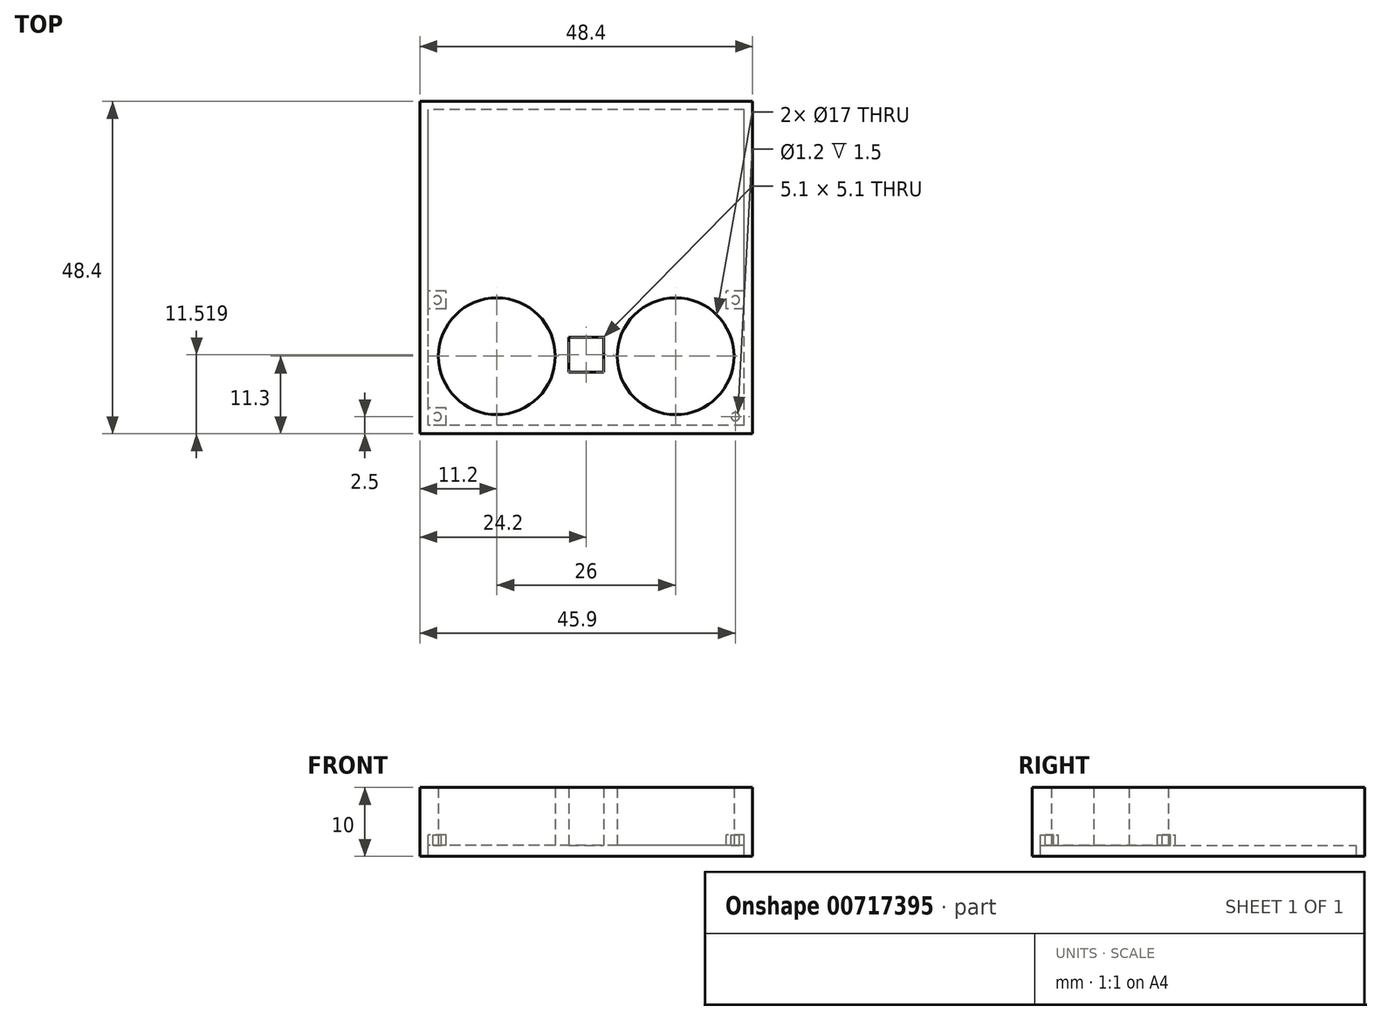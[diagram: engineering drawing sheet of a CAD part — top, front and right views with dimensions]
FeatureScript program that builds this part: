
annotation { "Feature Type Name" : "Feature", "Feature Type Description" : "" }
export const myFeature = defineFeature(function(context is Context, id is Id, definition is map)
    precondition{}
    {
        {
            var Q0;
            Q0=qCreatedBy(makeId("Top.planeOp"),FACE);
            var sketch = newSketch(context, id + "F0", { "sketchPlane" : qUnion([Q0])});
            skLineSegment(sketch, "E0.bottom", {"start": v(0, 0) * mm, "end": v(-23, 0) * mm});
            skLineSegment(sketch, "E0.top", {"start": v(0, 23) * mm, "end": v(-23, 23) * mm});
            skLineSegment(sketch, "E0.left", {"start": v(0, 0) * mm, "end": v(0, 23) * mm});
            skLineSegment(sketch, "E0.right", {"start": v(-23, 0) * mm, "end": v(-23, 23) * mm});
            skLineSegment(sketch, "E1.MirrorCS", {"start": v(-23, 0) * mm, "end": v(-23, -23) * mm});
            skLineSegment(sketch, "E2.MirrorCS", {"start": v(0, 0) * mm, "end": v(0, -23) * mm});
            skLineSegment(sketch, "E3.MirrorCS", {"start": v(0, -23) * mm, "end": v(-23, -23) * mm});
            skLineSegment(sketch, "E4.MirrorCS", {"start": v(0, 23) * mm, "end": v(23, 23) * mm});
            skLineSegment(sketch, "E5.MirrorCS", {"start": v(0, -23) * mm, "end": v(23, -23) * mm});
            skLineSegment(sketch, "E6.MirrorCS", {"start": v(23, 0) * mm, "end": v(23, 23) * mm});
            skLineSegment(sketch, "E7.MirrorCS", {"start": v(0, 0) * mm, "end": v(23, 0) * mm});
            skLineSegment(sketch, "E8.MirrorCS", {"start": v(23, 0) * mm, "end": v(23, -23) * mm});
            skCircle(sketch, "E9", {"center": v(13, -12.9) * mm, "radius": 8.5 * mm});
            skCircle(sketch, "E10", {"center": v(-13, -12.9) * mm, "radius": 8.5 * mm});
            skLineSegment(sketch, "E11.bottom", {"start": v(-2.55, -15.23) * mm, "end": v(2.55, -15.23) * mm});
            skLineSegment(sketch, "E11.top", {"start": v(-2.55, -10.13) * mm, "end": v(2.55, -10.13) * mm});
            skLineSegment(sketch, "E11.left", {"start": v(-2.55, -15.23) * mm, "end": v(-2.55, -10.13) * mm});
            skLineSegment(sketch, "E11.right", {"start": v(2.55, -15.23) * mm, "end": v(2.55, -10.13) * mm});
            skSolve(sketch);
        }
        {
            var Q0;
            {var subQ1=sQuery(id+"F0.wireOp",EDGE,"E0.top");Q0=makeQuery(id+"F0.imprint","IMPRINT",FACE,{"disambiguationData":[TD([[makeQuery(id+"F0.imprint","IMPRINT",EDGE,{"derivedFrom":subQ1}),1.0]])]});}
            var Q1;
            {var subQ1=sQuery(id+"F0.wireOp",EDGE,"E1.MirrorCS");Q1=makeQuery(id+"F0.imprint","IMPRINT",FACE,{"disambiguationData":[TD([[makeQuery(id+"F0.imprint","IMPRINT",EDGE,{"derivedFrom":subQ1}),1.0]])]});}
            var Q2;
            {var subQ7=sQuery(id+"F0.wireOp",EDGE,"E4.MirrorCS");Q2=makeQuery(id+"F0.imprint","IMPRINT",FACE,{"disambiguationData":[TD([[makeQuery(id+"F0.imprint","IMPRINT",EDGE,{"derivedFrom":subQ7}),-1.0]])]});}
            var Q3;
            {var subQ9=sQuery(id+"F0.wireOp",EDGE,"E5.MirrorCS");Q3=makeQuery(id+"F0.imprint","IMPRINT",FACE,{"disambiguationData":[TD([[makeQuery(id+"F0.imprint","IMPRINT",EDGE,{"derivedFrom":subQ9}),1.0]])]});}
            extrude(context, id + "F1", {"entities" : qUnion([Q0, Q1, Q2, Q3]), "endBound" : BoundingType.SYMMETRIC, "depth" : 1.2 * mm, "offsetDistance" : 25 * mm});
        }
        {
            var Q0;
            Q0=makeQuery(id+"F1.opExtrude","CAP_FACE",FACE,{"disambiguationData":[OSD([sQuery(id+"F0.wireOp",EDGE,"E0.top"),sQuery(id+"F0.wireOp",EDGE,"E0.right"),sQuery(id+"F0.wireOp",EDGE,"E1.MirrorCS"),sQuery(id+"F0.wireOp",EDGE,"E3.MirrorCS"),sQuery(id+"F0.wireOp",EDGE,"18OHl2Td-8SmV-nLja-3BuC-y3GKfxBrHoTz"),sQuery(id+"F0.wireOp",EDGE,"E4.MirrorCS"),sQuery(id+"F0.wireOp",EDGE,"f96b6ea1-77e4-4928-808a-502d4fa3524e1.MirrorC"),sQuery(id+"F0.wireOp",EDGE,"E5.MirrorCS"),sQuery(id+"F0.wireOp",EDGE,"E6.MirrorCS"),sQuery(id+"F0.wireOp",EDGE,"E8.MirrorCS"),sQuery(id+"F0.wireOp",EDGE,"ZzQ9hNgQ-oA48-EWd8-CxiW-ZcLfL0NBcqYF")])],"isStart":false});
            var sketch = newSketch(context, id + "F2", { "sketchPlane" : qUnion([Q0])});
            skLineSegment(sketch, "E12.0", {"start": v(23, 23) * mm, "end": v(-23, 23) * mm});
            skLineSegment(sketch, "E12.1", {"start": v(-23, -23) * mm, "end": v(-23, 23) * mm});
            skLineSegment(sketch, "E12.2", {"start": v(23, -23) * mm, "end": v(-23, -23) * mm});
            skLineSegment(sketch, "E12.3", {"start": v(23, -23) * mm, "end": v(23, 23) * mm});
            skPoint(sketch, "E12.4", {"position": v(0, 0) * mm});
            skLineSegment(sketch, "E13.bottom", {"start": v(0, 24.2) * mm, "end": v(-24.2, 24.2) * mm});
            skLineSegment(sketch, "E13.top", {"start": v(0, -24.2) * mm, "end": v(-24.2, -24.2) * mm});
            skLineSegment(sketch, "E13.left", {"start": v(0, 24.2) * mm, "end": v(0, -24.2) * mm});
            skLineSegment(sketch, "E13.right", {"start": v(-24.2, 24.2) * mm, "end": v(-24.2, -24.2) * mm});
            skLineSegment(sketch, "E14.MirrorCS", {"start": v(0, 24.2) * mm, "end": v(24.2, 24.2) * mm});
            skLineSegment(sketch, "E15.MirrorCS", {"start": v(24.2, 24.2) * mm, "end": v(24.2, -24.2) * mm});
            skLineSegment(sketch, "E16.MirrorCS", {"start": v(0, -24.2) * mm, "end": v(24.2, -24.2) * mm});
            skSolve(sketch);
        }
        {
            var Q0;
            {var subQ1=sQuery(id+"F2.wireOp",EDGE,"E12.1");Q0=makeQuery(id+"F2.imprint","IMPRINT",FACE,{"disambiguationData":[TD([[makeQuery(id+"F2.imprint","IMPRINT",EDGE,{"derivedFrom":subQ1}),1.0]])]});}
            var Q1;
            {var subQ4=sQuery(id+"F2.wireOp",EDGE,"E12.3");Q1=makeQuery(id+"F2.imprint","IMPRINT",FACE,{"disambiguationData":[TD([[makeQuery(id+"F2.imprint","IMPRINT",EDGE,{"derivedFrom":subQ4}),-1.0]])]});}
            extrude(context, id + "F3", {"entities" : qUnion([Q0, Q1]), "operationType" : NewBodyOperationType.ADD, "oppositeDirection" : true, "depth" : 10 * mm, "offsetDistance" : 25 * mm});
        }
        {
            var Q0;
            Q0=makeQuery(id+"F1.opExtrude","CAP_FACE",FACE,{"disambiguationData":[OSD([sQuery(id+"F0.wireOp",EDGE,"E0.top"),sQuery(id+"F0.wireOp",EDGE,"E0.right"),sQuery(id+"F0.wireOp",EDGE,"E1.MirrorCS"),sQuery(id+"F0.wireOp",EDGE,"E3.MirrorCS"),sQuery(id+"F0.wireOp",EDGE,"18OHl2Td-8SmV-nLja-3BuC-y3GKfxBrHoTz"),sQuery(id+"F0.wireOp",EDGE,"E4.MirrorCS"),sQuery(id+"F0.wireOp",EDGE,"f96b6ea1-77e4-4928-808a-502d4fa3524e1.MirrorC"),sQuery(id+"F0.wireOp",EDGE,"E5.MirrorCS"),sQuery(id+"F0.wireOp",EDGE,"E6.MirrorCS"),sQuery(id+"F0.wireOp",EDGE,"E8.MirrorCS"),sQuery(id+"F0.wireOp",EDGE,"ZzQ9hNgQ-oA48-EWd8-CxiW-ZcLfL0NBcqYF")])],"isStart":true});
            var sketch = newSketch(context, id + "F4", { "sketchPlane" : qUnion([Q0])});
            skLineSegment(sketch, "E17.0", {"start": v(23, 23) * mm, "end": v(-23, 23) * mm});
            skLineSegment(sketch, "E17.1", {"start": v(-23, 23) * mm, "end": v(-23, -23) * mm});
            skLineSegment(sketch, "E17.2", {"start": v(23, -23) * mm, "end": v(-23, -23) * mm});
            skLineSegment(sketch, "E17.3", {"start": v(23, 23) * mm, "end": v(23, -23) * mm});
            skLineSegment(sketch, "E18", {"start": v(-21.7, 23) * mm, "end": v(-21.7, 21.7) * mm, "construction": true});
            skLineSegment(sketch, "E19", {"start": v(-21.7, 21.7) * mm, "end": v(-23, 21.7) * mm, "construction": true});
            skCircle(sketch, "E20", {"center": v(-21.7, 21.7) * mm, "radius": 0.6 * mm});
            skCircle(sketch, "E21.MirrorC", {"center": v(21.7, 21.7) * mm, "radius": 0.6 * mm});
            skLineSegment(sketch, "E22.bottom", {"start": v(-20.4, 23) * mm, "end": v(-23, 23) * mm});
            skLineSegment(sketch, "E22.top", {"start": v(-20.4, 20.4) * mm, "end": v(-23, 20.4) * mm});
            skLineSegment(sketch, "E22.left", {"start": v(-20.4, 23) * mm, "end": v(-20.4, 20.4) * mm});
            skLineSegment(sketch, "E22.right", {"start": v(-23, 23) * mm, "end": v(-23, 20.4) * mm});
            skLineSegment(sketch, "E23.MirrorCS", {"start": v(20.4, 23) * mm, "end": v(20.4, 20.4) * mm});
            skLineSegment(sketch, "E24.MirrorCS", {"start": v(20.4, 20.4) * mm, "end": v(23, 20.4) * mm});
            skLineSegment(sketch, "E25", {"start": v(-21.7, 6) * mm, "end": v(-21.7, 4.7) * mm, "construction": true});
            skLineSegment(sketch, "E26", {"start": v(-21.7, 4.7) * mm, "end": v(-23, 4.7) * mm, "construction": true});
            skCircle(sketch, "E27", {"center": v(-21.7, 4.7) * mm, "radius": 0.6 * mm});
            skLineSegment(sketch, "E28.bottom", {"start": v(-20.4, 6) * mm, "end": v(-23, 6) * mm});
            skLineSegment(sketch, "E28.top", {"start": v(-20.4, 3.4) * mm, "end": v(-23, 3.4) * mm});
            skLineSegment(sketch, "E28.left", {"start": v(-20.4, 6) * mm, "end": v(-20.4, 3.4) * mm});
            skLineSegment(sketch, "E28.right", {"start": v(-23, 6) * mm, "end": v(-23, 3.4) * mm});
            skLineSegment(sketch, "E29", {"start": v(21.7, 6) * mm, "end": v(21.7, 4.7) * mm, "construction": true});
            skLineSegment(sketch, "E30", {"start": v(21.7, 4.7) * mm, "end": v(20.4, 4.7) * mm, "construction": true});
            skCircle(sketch, "E31", {"center": v(21.7, 4.7) * mm, "radius": 0.6 * mm});
            skLineSegment(sketch, "E32.bottom", {"start": v(23, 6) * mm, "end": v(20.4, 6) * mm});
            skLineSegment(sketch, "E32.top", {"start": v(23, 3.4) * mm, "end": v(20.4, 3.4) * mm});
            skLineSegment(sketch, "E32.left", {"start": v(23, 6) * mm, "end": v(23, 3.4) * mm});
            skLineSegment(sketch, "E32.right", {"start": v(20.4, 6) * mm, "end": v(20.4, 3.4) * mm});
            skSolve(sketch);
        }
        {
            var Q0;
            Q0=makeQuery(id+"F4.imprint","IMPRINT",FACE,{"disambiguationData":[TD([[makeQuery(id+"F4.imprint","IMPRINT",EDGE,{"derivedFrom":sQuery(id+"F4.wireOp",EDGE,"E21.MirrorC")}),1.0]])]});
            var Q1;
            Q1=makeQuery(id+"F4.imprint","IMPRINT",FACE,{"disambiguationData":[TD([[makeQuery(id+"F4.imprint","IMPRINT",EDGE,{"derivedFrom":sQuery(id+"F4.wireOp",EDGE,"E20")}),-1.0]])]});
            var Q2;
            Q2=makeQuery(id+"F4.imprint","IMPRINT",FACE,{"disambiguationData":[TD([[makeQuery(id+"F4.imprint","IMPRINT",EDGE,{"derivedFrom":sQuery(id+"F4.wireOp",EDGE,"E27")}),-1.0]])]});
            var Q3;
            Q3=makeQuery(id+"F4.imprint","IMPRINT",FACE,{"disambiguationData":[TD([[makeQuery(id+"F4.imprint","IMPRINT",EDGE,{"derivedFrom":sQuery(id+"F4.wireOp",EDGE,"E31")}),-1.0]])]});
            extrude(context, id + "F5", {"entities" : qUnion([Q0, Q1, Q2, Q3]), "operationType" : NewBodyOperationType.ADD, "depth" : 5.7 * mm, "offsetDistance" : 25 * mm});
        }
        {
            var Q0;
            Q0=makeQuery(id+"F5.boolean.opBoolean","SPLIT",FACE,{"disambiguationData":[TD([makeQuery(id+"F5.opExtrude","SWEPT_FACE",FACE,{"disambiguationData":[OSD([sQuery(id+"F4.wireOp",EDGE,"E27")])]})])],"derivedFrom":makeQuery(id+"F1.opExtrude","CAP_FACE",FACE,{"disambiguationData":[OSD([sQuery(id+"F0.wireOp",EDGE,"E0.top"),sQuery(id+"F0.wireOp",EDGE,"E0.right"),sQuery(id+"F0.wireOp",EDGE,"E1.MirrorCS"),sQuery(id+"F0.wireOp",EDGE,"E3.MirrorCS"),sQuery(id+"F0.wireOp",EDGE,"E4.MirrorCS"),sQuery(id+"F0.wireOp",EDGE,"E5.MirrorCS"),sQuery(id+"F0.wireOp",EDGE,"E6.MirrorCS"),sQuery(id+"F0.wireOp",EDGE,"E8.MirrorCS"),sQuery(id+"F0.wireOp",EDGE,"E9"),sQuery(id+"F0.wireOp",EDGE,"E10"),sQuery(id+"F0.wireOp",EDGE,"E11.bottom"),sQuery(id+"F0.wireOp",EDGE,"E11.top"),sQuery(id+"F0.wireOp",EDGE,"E11.left"),sQuery(id+"F0.wireOp",EDGE,"E11.right")])],"isStart":true})});
            var Q1;
            Q1=makeQuery(id+"F5.boolean.opBoolean","SPLIT",FACE,{"disambiguationData":[TD([makeQuery(id+"F5.opExtrude","SWEPT_FACE",FACE,{"disambiguationData":[OSD([sQuery(id+"F4.wireOp",EDGE,"E20")])]})])],"derivedFrom":makeQuery(id+"F1.opExtrude","CAP_FACE",FACE,{"disambiguationData":[OSD([sQuery(id+"F0.wireOp",EDGE,"E0.top"),sQuery(id+"F0.wireOp",EDGE,"E0.right"),sQuery(id+"F0.wireOp",EDGE,"E1.MirrorCS"),sQuery(id+"F0.wireOp",EDGE,"E3.MirrorCS"),sQuery(id+"F0.wireOp",EDGE,"E4.MirrorCS"),sQuery(id+"F0.wireOp",EDGE,"E5.MirrorCS"),sQuery(id+"F0.wireOp",EDGE,"E6.MirrorCS"),sQuery(id+"F0.wireOp",EDGE,"E8.MirrorCS"),sQuery(id+"F0.wireOp",EDGE,"E9"),sQuery(id+"F0.wireOp",EDGE,"E10"),sQuery(id+"F0.wireOp",EDGE,"E11.bottom"),sQuery(id+"F0.wireOp",EDGE,"E11.top"),sQuery(id+"F0.wireOp",EDGE,"E11.left"),sQuery(id+"F0.wireOp",EDGE,"E11.right")])],"isStart":true})});
            var Q2;
            Q2=makeQuery(id+"F5.boolean.opBoolean","SPLIT",FACE,{"disambiguationData":[TD([makeQuery(id+"F5.opExtrude","SWEPT_FACE",FACE,{"disambiguationData":[OSD([sQuery(id+"F4.wireOp",EDGE,"E21.MirrorC")])]})])],"derivedFrom":makeQuery(id+"F1.opExtrude","CAP_FACE",FACE,{"disambiguationData":[OSD([sQuery(id+"F0.wireOp",EDGE,"E0.top"),sQuery(id+"F0.wireOp",EDGE,"E0.right"),sQuery(id+"F0.wireOp",EDGE,"E1.MirrorCS"),sQuery(id+"F0.wireOp",EDGE,"E3.MirrorCS"),sQuery(id+"F0.wireOp",EDGE,"E4.MirrorCS"),sQuery(id+"F0.wireOp",EDGE,"E5.MirrorCS"),sQuery(id+"F0.wireOp",EDGE,"E6.MirrorCS"),sQuery(id+"F0.wireOp",EDGE,"E8.MirrorCS"),sQuery(id+"F0.wireOp",EDGE,"E9"),sQuery(id+"F0.wireOp",EDGE,"E10"),sQuery(id+"F0.wireOp",EDGE,"E11.bottom"),sQuery(id+"F0.wireOp",EDGE,"E11.top"),sQuery(id+"F0.wireOp",EDGE,"E11.left"),sQuery(id+"F0.wireOp",EDGE,"E11.right")])],"isStart":true})});
            var Q3;
            Q3=makeQuery(id+"F5.boolean.opBoolean","SPLIT",FACE,{"disambiguationData":[TD([makeQuery(id+"F5.opExtrude","SWEPT_FACE",FACE,{"disambiguationData":[OSD([sQuery(id+"F4.wireOp",EDGE,"E31")])]})])],"derivedFrom":makeQuery(id+"F1.opExtrude","CAP_FACE",FACE,{"disambiguationData":[OSD([sQuery(id+"F0.wireOp",EDGE,"E0.top"),sQuery(id+"F0.wireOp",EDGE,"E0.right"),sQuery(id+"F0.wireOp",EDGE,"E1.MirrorCS"),sQuery(id+"F0.wireOp",EDGE,"E3.MirrorCS"),sQuery(id+"F0.wireOp",EDGE,"E4.MirrorCS"),sQuery(id+"F0.wireOp",EDGE,"E5.MirrorCS"),sQuery(id+"F0.wireOp",EDGE,"E6.MirrorCS"),sQuery(id+"F0.wireOp",EDGE,"E8.MirrorCS"),sQuery(id+"F0.wireOp",EDGE,"E9"),sQuery(id+"F0.wireOp",EDGE,"E10"),sQuery(id+"F0.wireOp",EDGE,"E11.bottom"),sQuery(id+"F0.wireOp",EDGE,"E11.top"),sQuery(id+"F0.wireOp",EDGE,"E11.left"),sQuery(id+"F0.wireOp",EDGE,"E11.right")])],"isStart":true})});
            extrude(context, id + "F6", {"entities" : qUnion([Q0, Q1, Q2, Q3]), "operationType" : NewBodyOperationType.ADD, "depth" : 7.2 * mm, "offsetDistance" : 25 * mm});
        }
    });
